# Revit family: Gleitstreifen PA 6
name_source: partatom
category: HLS-Bauteile
revit_build: Autodesk Revit 2017 (Build: 20190507_1515(x64)
units: mm (PartAtom-declared; Revit-internal decimal feet)

## family parameters
Arbeitsebenenbasiert = Ja
Beim Laden mit Abzugskörper schneiden = Nein
Bemaßung runder Anschluss = Durchmesser verwenden
Gemeinsam genutzt = Ja
Immer vertikal = Nein
Raumberechnungspunkt = Nein
Teiletyp = Normal

## types (4) — shared parameters
Anzahl Befestigungsloch = 2 St
B = 50 mm  [stored 0.164042 ft]
Breite = 50 mm  [stored 0.164042 ft]
D = 11 mm
Fabrikat = MEFA
Firma = MEFA Befestigungs- und Montagesysteme GmbH
Haftreibungsfaktor = 0,2 - 0,3
Kurztext1 = Gleitstreifen PA 6 2-fach gelocht
Lochdurchmesser = 10 mm
Mengeneinheit = St
Stärke = 5 mm  [stored 0.0164042 ft]
Vorgabe-Ansicht = 1219 mm
max. Temperaturbeständigkeit = 110 °C
vpe = 1 St

## per-type parameters (varying)
| type | Abmessung | Artikelnummer | EAN | Gewicht | Gewicht pro Bauteil | Kurztext2 | L | L1 | Lochabstand | Länge | für Gleitplattenbreite |
| Gleitstreifen PA 6, 2x gelocht, 163x 50x 5 | 163 x 50 x 5 mm | 077955501 | 4250928448613 | 0.05 kg | 0.05 kg | für Breite 100 mm 163 x 50 x 5 mm | 163 mm  [stored 0.534777 ft] | 138 mm  [stored 0.452756 ft] | 138 mm | 163 mm  [stored 0.534777 ft] | 100 mm |
| Gleitstreifen PA 6, 2x gelocht, 213x 50x 5 | 213 x 50 x 5 mm | 077956701 | 4250928448620 | 0.06 kg | 0.06 kg | für Breite 150 mm 213 x 50 x 5 mm | 213 mm  [stored 0.698819 ft] | 188 mm  [stored 0.616798 ft] | 188 mm | 213 mm  [stored 0.698819 ft] | 150 mm |
| Gleitstreifen PA 6, 2x gelocht, 263x 50x 5 | 263 x 50 x 5 mm | 077956001 | 4250928448637 | 0.07 kg | 0.07 kg | für Breite 200 mm 263 x 50 x 5 mm | 263 mm  [stored 0.862861 ft] | 238 mm  [stored 0.78084 ft] | 238 mm | 263 mm  [stored 0.862861 ft] | 200 mm |
| Gleitstreifen PA 6, 2x gelocht, 313x 50x 5 | 313 x 50 x 5 mm | 077957001 | 4250928448644 | 0.09 kg | 0.09 kg | für Breite 250 mm 313 x 50 x 5 mm | 313 mm  [stored 1.0269 ft] | 288 mm  [stored 0.944882 ft] | 288 mm | 313 mm  [stored 1.0269 ft] | 250 mm |

note: [stored X ft] marks values corroborated as IEEE doubles in the binary element streams (Revit-internal decimal feet)
